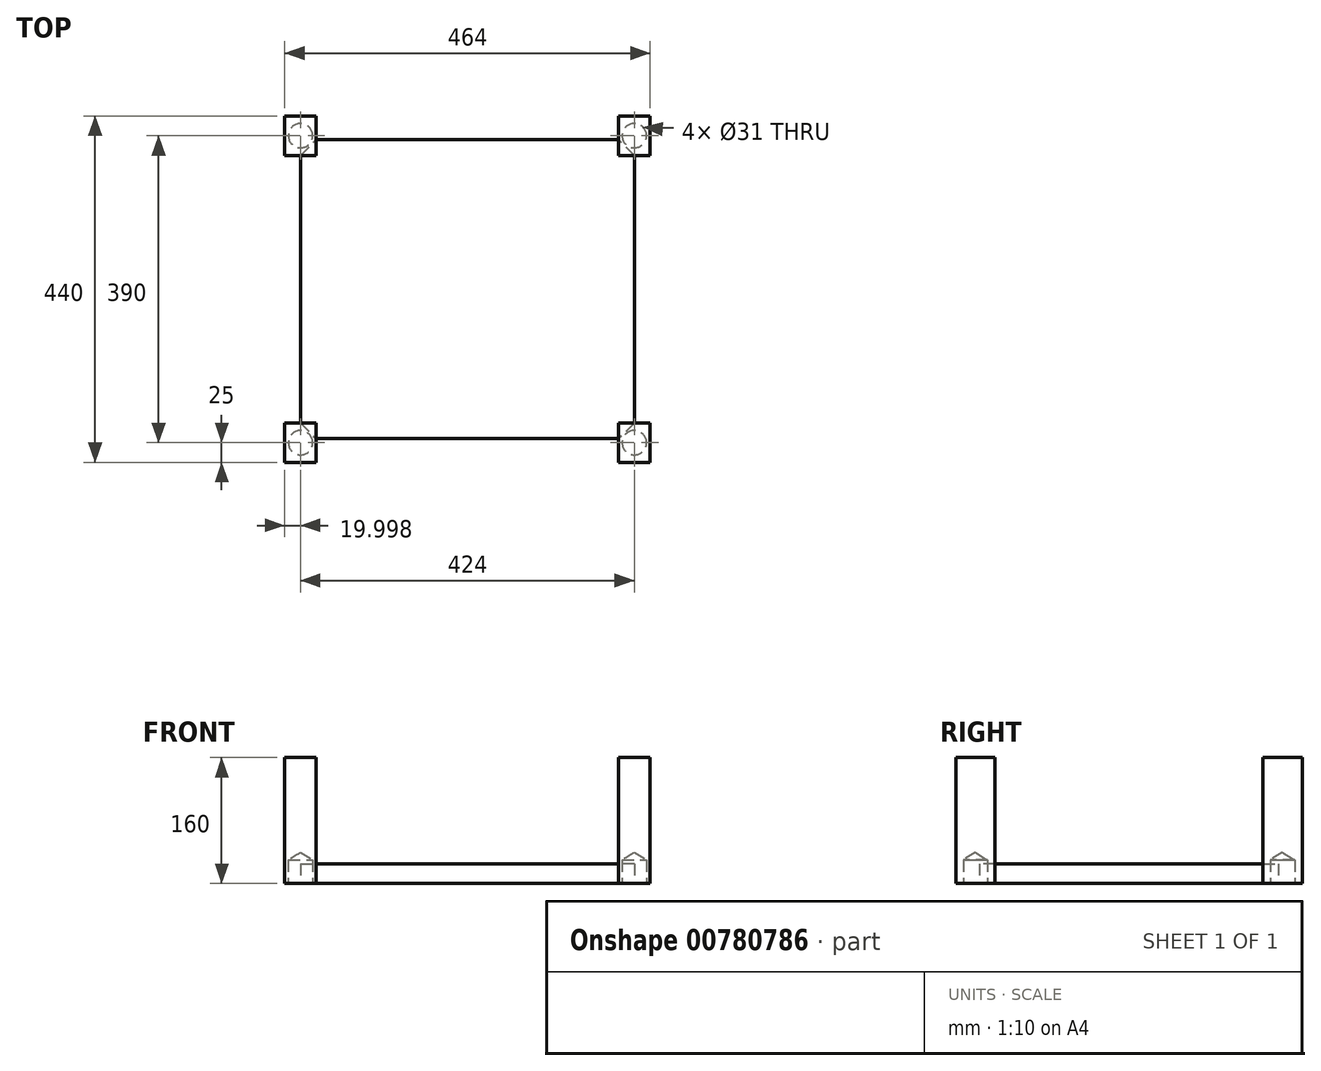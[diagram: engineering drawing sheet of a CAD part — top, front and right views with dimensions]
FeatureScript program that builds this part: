
annotation { "Feature Type Name" : "Feature", "Feature Type Description" : "" }
export const myFeature = defineFeature(function(context is Context, id is Id, definition is map)
    precondition{}
    {
        {
            var Q0;
            Q0=qCreatedBy(makeId("Top.planeOp"),FACE);
            var sketch = newSketch(context, id + "F0", { "sketchPlane" : qUnion([Q0])});
            skLineSegment(sketch, "E0.0.0", {"start": v(161.97, -320.77) * mm, "end": v(161.97, -270.77) * mm, "construction": true});
            skLineSegment(sketch, "E0.0.1", {"start": v(161.97, -270.77) * mm, "end": v(121.97, -270.77) * mm, "construction": true});
            skLineSegment(sketch, "E0.0.2", {"start": v(121.97, -270.77) * mm, "end": v(121.97, -320.77) * mm, "construction": true});
            skLineSegment(sketch, "E0.0.3", {"start": v(121.97, -320.77) * mm, "end": v(161.97, -320.77) * mm, "construction": true});
            skLineSegment(sketch, "E1.0.0", {"start": v(-262.03, -320.77) * mm, "end": v(-262.03, -270.77) * mm, "construction": true});
            skLineSegment(sketch, "E1.0.1", {"start": v(-262.03, -270.77) * mm, "end": v(-302.03, -270.77) * mm, "construction": true});
            skLineSegment(sketch, "E1.0.2", {"start": v(-302.03, -270.77) * mm, "end": v(-302.03, -320.77) * mm, "construction": true});
            skLineSegment(sketch, "E1.0.3", {"start": v(-302.03, -320.77) * mm, "end": v(-262.03, -320.77) * mm, "construction": true});
            skLineSegment(sketch, "E2.0.0", {"start": v(-302.03, 69.23) * mm, "end": v(-262.03, 69.23) * mm, "construction": true});
            skLineSegment(sketch, "E2.0.1", {"start": v(-262.03, 69.23) * mm, "end": v(-262.03, 119.23) * mm, "construction": true});
            skLineSegment(sketch, "E2.0.2", {"start": v(-262.03, 119.23) * mm, "end": v(-302.03, 119.23) * mm, "construction": true});
            skLineSegment(sketch, "E2.0.3", {"start": v(-302.03, 119.23) * mm, "end": v(-302.03, 69.23) * mm, "construction": true});
            skLineSegment(sketch, "E3.0.0", {"start": v(161.97, 119.23) * mm, "end": v(121.97, 119.23) * mm, "construction": true});
            skLineSegment(sketch, "E3.0.1", {"start": v(121.97, 119.23) * mm, "end": v(121.97, 69.23) * mm, "construction": true});
            skLineSegment(sketch, "E3.0.2", {"start": v(121.97, 69.23) * mm, "end": v(161.97, 69.23) * mm, "construction": true});
            skLineSegment(sketch, "E3.0.3", {"start": v(161.97, 69.23) * mm, "end": v(161.97, 119.23) * mm, "construction": true});
            skCircle(sketch, "E4", {"center": v(141.97, 94.23) * mm, "radius": 15 * mm});
            skPoint(sketch, "E4.centerSnap0", {"position": v(121.97, 94.23) * mm});
            skPoint(sketch, "E4.centerSnap1", {"position": v(141.97, 69.23) * mm});
            skCircle(sketch, "E5.MirrorC", {"center": v(-282.03, 94.23) * mm, "radius": 15 * mm});
            skCircle(sketch, "E6.MirrorC", {"center": v(141.97, -295.77) * mm, "radius": 15 * mm});
            skCircle(sketch, "E7.MirrorC", {"center": v(-282.03, -295.77) * mm, "radius": 15 * mm});
            skSolve(sketch);
        }
        {
            var Q0;
            Q0=qCreatedBy(makeId("Top.planeOp"),FACE);
            var sketch = newSketch(context, id + "F1", { "sketchPlane" : qUnion([Q0])});
            skLineSegment(sketch, "E8.0", {"start": v(-302.03, 69.23) * mm, "end": v(-262.03, 69.23) * mm});
            skPoint(sketch, "E9.0", {"position": v(-302.03, 94.23) * mm});
            skPoint(sketch, "E10.0", {"position": v(-282.03, 119.23) * mm});
            skLineSegment(sketch, "E11.0", {"start": v(-262.03, 69.23) * mm, "end": v(-262.03, 119.23) * mm});
            skLineSegment(sketch, "E12.0", {"start": v(-262.03, 119.23) * mm, "end": v(-302.03, 119.23) * mm});
            skLineSegment(sketch, "E13.0", {"start": v(-302.03, 119.23) * mm, "end": v(-302.03, 69.23) * mm});
            skLineSegment(sketch, "E14.0", {"start": v(161.97, 119.23) * mm, "end": v(121.97, 119.23) * mm});
            skLineSegment(sketch, "E15.0", {"start": v(121.97, 119.23) * mm, "end": v(121.97, 69.23) * mm});
            skLineSegment(sketch, "E16.0", {"start": v(121.97, 69.23) * mm, "end": v(161.97, 69.23) * mm});
            skLineSegment(sketch, "E17.0", {"start": v(161.97, 69.23) * mm, "end": v(161.97, 119.23) * mm});
            skLineSegment(sketch, "E18.0", {"start": v(161.97, -320.77) * mm, "end": v(161.97, -270.77) * mm});
            skLineSegment(sketch, "E19.0", {"start": v(161.97, -270.77) * mm, "end": v(121.97, -270.77) * mm});
            skLineSegment(sketch, "E20.0", {"start": v(121.97, -320.77) * mm, "end": v(161.97, -320.77) * mm});
            skLineSegment(sketch, "E21.0", {"start": v(121.97, -270.77) * mm, "end": v(121.97, -320.77) * mm});
            skLineSegment(sketch, "E22.0", {"start": v(-262.03, -270.77) * mm, "end": v(-302.03, -270.77) * mm});
            skLineSegment(sketch, "E23.0", {"start": v(-262.03, -320.77) * mm, "end": v(-262.03, -270.77) * mm});
            skLineSegment(sketch, "E24.0", {"start": v(-302.03, -320.77) * mm, "end": v(-262.03, -320.77) * mm});
            skLineSegment(sketch, "E25.0", {"start": v(-302.03, -270.77) * mm, "end": v(-302.03, -320.77) * mm});
            skSolve(sketch);
        }
        {
            var Q0;
            Q0 = qSketchRegion(id + "F1", true);
            extrude(context, id + "F2", {"entities" : qUnion([Q0]), "depth" : 160 * mm, "offsetDistance" : 25 * mm});
        }
        {
            var Q0;
            Q0=makeQuery(id+"F2.opExtrude","CAP_FACE",FACE,{"disambiguationData":[OSD([sQuery(id+"F1.wireOp",EDGE,"E22.0"),sQuery(id+"F1.wireOp",EDGE,"E23.0"),sQuery(id+"F1.wireOp",EDGE,"E24.0"),sQuery(id+"F1.wireOp",EDGE,"E25.0")])],"isStart":true});
            var sketch = newSketch(context, id + "F3", { "sketchPlane" : qUnion([Q0])});
            skCircle(sketch, "E26.0", {"center": v(-282.03, 295.77) * mm, "radius": 15 * mm});
            skCircle(sketch, "E27.0", {"center": v(-282.03, -94.23) * mm, "radius": 15 * mm});
            skCircle(sketch, "E28.0", {"center": v(141.97, -94.23) * mm, "radius": 15 * mm});
            skCircle(sketch, "E29.0", {"center": v(141.97, 295.77) * mm, "radius": 15 * mm});
            skSolve(sketch);
        }
        {
            var Q0;
            Q0=sQuery(id+"F0.wireOp",VERTEX,"E7.MirrorC.center");
            var Q1;
            Q1=sQuery(id+"F0.wireOp",VERTEX,"E5.MirrorC.center");
            var Q2;
            Q2=sQuery(id+"F0.wireOp",VERTEX,"E4.center");
            var Q3;
            Q3=sQuery(id+"F0.wireOp",VERTEX,"E6.MirrorC.center");
            var Q4;
            Q4=makeQuery(id+"F2.opExtrude","SWEPT_BODY",BODY,{"disambiguationData":[OSD([sQuery(id+"F1.wireOp",EDGE,"E22.0"),sQuery(id+"F1.wireOp",EDGE,"E23.0"),sQuery(id+"F1.wireOp",EDGE,"E24.0"),sQuery(id+"F1.wireOp",EDGE,"E25.0")])]});
            var Q5;
            Q5=makeQuery(id+"F2.opExtrude","SWEPT_BODY",BODY,{"disambiguationData":[OSD([sQuery(id+"F1.wireOp",EDGE,"E8.0"),sQuery(id+"F1.wireOp",EDGE,"E11.0"),sQuery(id+"F1.wireOp",EDGE,"E12.0"),sQuery(id+"F1.wireOp",EDGE,"E13.0")])]});
            var Q6;
            Q6=makeQuery(id+"F2.opExtrude","SWEPT_BODY",BODY,{"disambiguationData":[OSD([sQuery(id+"F1.wireOp",EDGE,"E14.0"),sQuery(id+"F1.wireOp",EDGE,"E15.0"),sQuery(id+"F1.wireOp",EDGE,"E16.0"),sQuery(id+"F1.wireOp",EDGE,"E17.0")])]});
            var Q7;
            Q7=makeQuery(id+"F2.opExtrude","SWEPT_BODY",BODY,{"disambiguationData":[OSD([sQuery(id+"F1.wireOp",EDGE,"E18.0"),sQuery(id+"F1.wireOp",EDGE,"E19.0"),sQuery(id+"F1.wireOp",EDGE,"E20.0"),sQuery(id+"F1.wireOp",EDGE,"E21.0")])]});
            hole(context, id + "F4", {"style" : HoleStyle.SIMPLE, "endStyle" : HoleEndStyle.BLIND, "oppositeDirection" : true, "holeDiameter" : 31 * mm, "majorDiameter" : 5 * mm, "holeDepth" : 30 * mm, "isTappedThrough" : true, "tappedDepth" : 12 * mm, "tapClearance" : 3, "locations" : qUnion([Q0, Q1, Q2, Q3]), "scope" : qUnion([Q4, Q5, Q6, Q7])});
        }
        {
            var Q0;
            Q0=makeQuery(id+"F3.imprint","IMPRINT",FACE,{"disambiguationData":[TD([[makeQuery(id+"F3.imprint","IMPRINT",EDGE,{"derivedFrom":sQuery(id+"F3.wireOp",EDGE,"E26.0")}),1.0]])]});
            var sketch = newSketch(context, id + "F5", { "sketchPlane" : qUnion([Q0])});
            skLineSegment(sketch, "E30.0.0", {"start": v(-282.03, 270.77) * mm, "end": v(-262.03, 270.77) * mm});
            skLineSegment(sketch, "E30.0.1", {"start": v(-262.03, 270.77) * mm, "end": v(-262.03, 290.77) * mm});
            skLineSegment(sketch, "E30.0.2", {"start": v(-262.03, 320.77) * mm, "end": v(-302.03, 320.77) * mm, "construction": true});
            skLineSegment(sketch, "E30.0.3", {"start": v(-302.03, 320.77) * mm, "end": v(-302.03, 270.77) * mm, "construction": true});
            skLineSegment(sketch, "E31.0.0", {"start": v(-302.03, -119.23) * mm, "end": v(-262.03, -119.23) * mm, "construction": true});
            skLineSegment(sketch, "E31.0.1", {"start": v(-262.03, -89.23) * mm, "end": v(-262.03, -69.23) * mm});
            skLineSegment(sketch, "E31.0.2", {"start": v(-262.03, -69.23) * mm, "end": v(-282.03, -69.23) * mm});
            skLineSegment(sketch, "E31.0.3", {"start": v(-302.03, -69.23) * mm, "end": v(-302.03, -119.23) * mm, "construction": true});
            skLineSegment(sketch, "E32.0.0", {"start": v(141.97, -69.23) * mm, "end": v(121.97, -69.23) * mm});
            skLineSegment(sketch, "E32.0.1", {"start": v(121.97, -69.23) * mm, "end": v(121.97, -94.23) * mm});
            skLineSegment(sketch, "E32.0.2", {"start": v(121.97, -119.23) * mm, "end": v(161.97, -119.23) * mm, "construction": true});
            skLineSegment(sketch, "E32.0.3", {"start": v(161.97, -119.23) * mm, "end": v(161.97, -69.23) * mm, "construction": true});
            skLineSegment(sketch, "E33.0.0", {"start": v(121.97, 270.77) * mm, "end": v(141.97, 270.77) * mm});
            skLineSegment(sketch, "E33.0.1", {"start": v(161.97, 270.77) * mm, "end": v(161.97, 320.77) * mm, "construction": true});
            skLineSegment(sketch, "E33.0.2", {"start": v(161.97, 320.77) * mm, "end": v(121.97, 320.77) * mm, "construction": true});
            skLineSegment(sketch, "E33.0.3", {"start": v(121.97, 290.77) * mm, "end": v(121.97, 270.77) * mm});
            skLineSegment(sketch, "E34", {"start": v(121.97, 290.77) * mm, "end": v(-262.03, 290.77) * mm});
            skLineSegment(sketch, "E35", {"start": v(-282.03, 270.77) * mm, "end": v(-282.03, -69.23) * mm});
            skLineSegment(sketch, "E36", {"start": v(-262.03, -89.23) * mm, "end": v(121.97, -89.23) * mm});
            skPoint(sketch, "E36.endSnap0", {"position": v(121.97, -94.23) * mm});
            skLineSegment(sketch, "E37", {"start": v(141.97, -69.23) * mm, "end": v(141.97, 270.77) * mm});
            skLineSegment(sketch, "E38", {"start": v(141.97, 270.77) * mm, "end": v(121.97, 290.77) * mm});
            skLineSegment(sketch, "E39", {"start": v(141.97, -69.23) * mm, "end": v(121.97, -89.23) * mm});
            skLineSegment(sketch, "E40", {"start": v(-282.03, -69.23) * mm, "end": v(-262.03, -89.23) * mm});
            skLineSegment(sketch, "E41", {"start": v(-282.03, 270.77) * mm, "end": v(-262.03, 290.77) * mm});
            skSolve(sketch);
        }
        {
            var Q0;
            Q0 = qSketchRegion(id + "F5", true);
            extrude(context, id + "F6", {"entities" : qUnion([Q0]), "oppositeDirection" : true, "depth" : 25 * mm, "offsetDistance" : 25 * mm});
        }
    });
